# Revit family: Reece_Tap_Milli_Inox_Basin Mixer_Extended_211 mm
name_source: partatom
category: Plumbing Fixtures
revit_build: Autodesk Revit 2018 (Build: 20190510_1515(x64)
units: mm (PartAtom-declared; Revit-internal decimal feet)

## family parameters
Cut with Voids When Loaded = No
Host = Face
Part Type = Normal
Room Calculation Point = Yes
Round Connector Dimension = Use Diameter
Shared = Yes

## types (1)
- Brushed Stainless Steel
    CW Connection = No
    CWFU = 0
    Default Elevation = 1000 mm  [stored 3.28084 ft]
    Description = Milli Inox Extended Basin Mixer Tap Stainless Steel (5 Star)
    Disclaimer = THIS FILE IS THE PROPERTY OF THE REECE GROUP. IT MAY NOT BE REPRODUCED, REVERSE-ENGINEERED OR MODIFIED. ANY REPUBLICATION, TRANSMISSION OR DISTRIBUTION FOR THE PURPOSE OF COMMERCIALLY EXPLOITING THE FILES IS PROHIBITED.
    HW Connection = No
    HWFU = 0
    Keynote = Product #2252110, Reece_Tap_Milli_Inox_Basin Mixer_Extended_211 mm - Brushed Stainless Steel
    Manufacturer = Milli
    Model = Inox
    Reece_Detail_Additional = Extended
    Reece_Detail_Disclaimer = THIS FILE IS THE PROPERTY OF THE REECE GROUP. IT MAY NOT BE REPRODUCED, REVERSE-ENGINEERED OR MODIFIED. ANY REPUBLICATION, TRANSMISSION OR DISTRIBUTION FOR THE PURPOSE OF COMMERCIALLY EXPLOITING THE FILES IS PROHIBITED.
    Reece_Material_Main = Reece_Brass_Brushed Stainless Steel
    Reece_Material_Secondary = Reece_Brass_Brushed Stainless Steel
    Reece_Overall_Diameter = 56 mm  [stored 0.183727 ft]
    Reece_Overall_Height = 294 mm  [stored 0.964567 ft]
    Reece_Overall_Length = 70 mm  [stored 0.229659 ft]
    Reece_Overall_Projection = 250 mm
    Reece_Product_Brand = Milli
    Reece_Product_Description = Milli Inox Extended Basin Mixer Tap Stainless Steel (5 Star)
    Reece_Product_Mount = Hob Mounted
    Reece_Product_Number = 2252110
    Reece_Product_Sub Brand = Inox
    Reece_Product_Type = Tap
    Reece_Product_Web Page = https://www.reece.com.au
    Reece_Tap_Clearance = 202 mm
    Reece_Tap_Inlet = 12 mm  [stored 0.0393701 ft]
    Reece_Tap_Reach = 211 mm  [stored 0.692257 ft]
    Type Comments = Tap
    URL = https://www.reece.com.au
    Vent Connection = No
    WFU = 0
    Waste Connection = No

note: [stored X ft] marks values corroborated as IEEE doubles in the binary element streams (Revit-internal decimal feet)

## geometry (parser evidence)
native form markers: Sweep x2
no freeform markers — native parametric forms only
